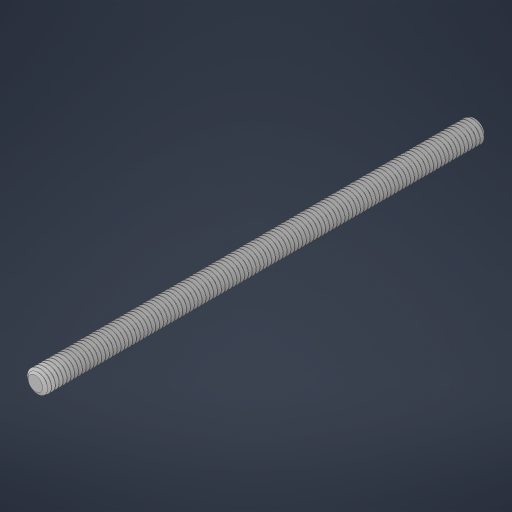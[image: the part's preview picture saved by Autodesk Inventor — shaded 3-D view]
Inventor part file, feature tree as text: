
AUTODESK INVENTOR PART (.ipt)
format: ipt  version: 2023 (Build 270158000, 158)  size: 2,834,432 bytes
history: native  units: in
note: dims shown in document units (in); Inventor stores cm internally (conversion verified against a paired STEP export)
features: mirror x1
ambient origin geometry x8: Origin, YZ Plane, XZ Plane, XY Plane, X Axis, Y Axis, Z Axis, Center Point
bodies: Solid1 (feature_tree)
feature tree (1):
  mirror  "Mirror1"
